# Revit family: Casement_36_E_Side_Hung_Standard
name_source: partatom
category: Windows
revit_build: Autodesk Revit 2014 (Build: 20130308_1515(x64)
units: mm (PartAtom-declared; Revit-internal decimal feet)

## types (18) — shared parameters
Aluminium Thickness = 1 mm  [stored 0.00328084 ft]
Area Pane Left Top = 0.52 m²
Bead SG Gap = 13 mm  [stored 0.0426509 ft]
Casement Dimension = 36 mm  [stored 0.11811 ft]
Custom Sash Height = 1154 mm  [stored 3.78609 ft]
Custom Sash Width = 554 mm  [stored 1.81759 ft]
DG Extrusion Start = 8 mm  [stored 0.0262467 ft]
DG Gasket Finish = Double Glazing Gasket Material
DG Thickness Calc = 4 mm  [stored 0.0131234 ft]
Default Sill Height = 800 mm  [stored 2.62467 ft]
Depth Bead = 22 mm  [stored 0.0721785 ft]
Description = Window 36mm, Type E side hung
Frame Center Offset = 18 mm  [stored 0.0590551 ft]
Height Panel 1 = 1139 mm  [stored 3.73688 ft]
Height Sash = 1124 mm  [stored 3.68766 ft]
Height Sash Opening = 1154 mm  [stored 3.78609 ft]
Length Transom = 540 mm  [stored 1.77165 ft]
Limit Fixed Pane Height Max = 1800 mm
Limit Fixed Pane Height Min = 200 mm  [stored 0.656168 ft]
Limit Fixed Pane Width Max = 1500 mm
Limit Fixed Pane Width Min = 200 mm  [stored 0.656168 ft]
Limit Sash Height Max = 1300 mm  [stored 4.26509 ft]
Limit Sash Height Min = 300 mm  [stored 0.984252 ft]
Limit Sash Width Max = 600 mm  [stored 1.9685 ft]
Limit Sash Width Min = 300 mm  [stored 0.984252 ft]
Limit Window Height Max = 1860 mm
Limit Window Height Min = 1430 mm  [stored 4.6916 ft]
Limit Window Width Max = 2130 mm
Limit Window Width Min = 830 mm  [stored 2.7231 ft]
Manufacturer = Crealco
Max System DG One Piece Thickness = 6 mm  [stored 0.019685 ft]
Max System DG Unit Thickness = 25 mm  [stored 0.082021 ft]
Model = Casement 36
Offset Bead SG Center Reversed = 18 mm  [stored 0.0590551 ft]
Offset Mullion Left = 570 mm  [stored 1.87008 ft]
Offset Panel 3 Bead Top = 1200 mm
Offset Panel 4 Left = 600 mm  [stored 1.9685 ft]
Offset Sash Left = 23 mm  [stored 0.0754593 ft]
Offset Sash Top = 23 mm  [stored 0.0754593 ft]
Offset Transom Top = 1170 mm
Offset Window Exterior = 18 mm  [stored 0.0590551 ft]
SG Gasket Thickness = 6 mm  [stored 0.019685 ft]
Sash Center Offset = 15 mm  [stored 0.0492126 ft]
Sash Overlap = 7 mm  [stored 0.0229659 ft]
Sash Spacing Inner = 8 mm  [stored 0.0262467 ft]
URL = http://www.crealco.co.za
Wall Closure = By host
Width Bead = 15 mm  [stored 0.0492126 ft]
Width Fixed Pane Bottom LHS = 540 mm  [stored 1.77165 ft]
Width Panel 1 = 540 mm  [stored 1.77165 ft]
Width Profile = 30 mm  [stored 0.0984252 ft]
Width Sash = 524 mm  [stored 1.71916 ft]
Width Sash Opening = 554 mm  [stored 1.81759 ft]
zero-valued in all types: Window Exterior Offset

## per-type parameters (varying)
- 36-0915S-1000Pa: Area Pane Left Bottom=0.13 m²; Area Pane Right=0.36 m²; Clearvue Insulated LowE SHGC Value=0.5; Clearvue Insulated LowE U Value=4.02; Clearvue Insulated SHGC Value=0.549; Clearvue Insulated U Value=4.53; Clearvue SHGC Value=0.622; Clearvue U Value=6.69; Custom Windload=1000 mm  [stored 3.28084 ft]; Custom Window Height=1490 mm; Custom Window Width=890 mm  [stored 2.91995 ft]; Depth Mullion=37 mm  [stored 0.121391 ft]; Energy Advantage SHGC Value=0.558; Energy Advantage U Value=5.22; Height=1490 mm; Height Fixed Pane Bottom LHS=260 mm  [stored 0.853018 ft]; Height Fixed Pane RHS=1430 mm  [stored 4.6916 ft]; Intruderprufe Insulated LowE SHGC Value=0.46; Intruderprufe Insulated LowE U Value=3.93; Intruderprufe Insulated SHGC Value=0.501; Intruderprufe Insulated U Value=4.41; Intruderprufe LowE SHGC Value=0.525; Intruderprufe LowE U Value=5.09; Intruderprufe SHGC Value=0.593; Intruderprufe U Value=6.53; Length Mullion=1490 mm; Max Pane Area=0.52 m²; Mullion Depth Windload Based=37 mm  [stored 0.121391 ft]; Width=890 mm  [stored 2.91995 ft]; Width Fixed Pane RHS=260 mm  [stored 0.853018 ft]; Windload Design=1000 mm  [stored 3.28084 ft]
- 36-1215S-1000Pa: Area Pane Left Bottom=0.13 m²; Area Pane Right=0.78 m²; Clearvue Insulated LowE SHGC Value=0.564; Clearvue Insulated LowE U Value=3.83; Clearvue Insulated SHGC Value=0.62; Clearvue Insulated U Value=4.43; Clearvue SHGC Value=0.704; Clearvue U Value=6.89; Custom Windload=1000 mm  [stored 3.28084 ft]; Custom Window Height=1490 mm; Custom Window Width=1190 mm  [stored 3.9042 ft]; Depth Mullion=54 mm  [stored 0.177165 ft]; Energy Advantage SHGC Value=0.631; Energy Advantage U Value=5.2; Height=1490 mm; Height Fixed Pane Bottom LHS=260 mm  [stored 0.853018 ft]; Height Fixed Pane RHS=1430 mm  [stored 4.6916 ft]; Intruderprufe Insulated LowE SHGC Value=0.521; Intruderprufe Insulated LowE U Value=3.75; Intruderprufe Insulated SHGC Value=0.569; Intruderprufe Insulated U Value=4.32; Intruderprufe LowE SHGC Value=0.59; Intruderprufe LowE U Value=5.09; Intruderprufe SHGC Value=0.671; Intruderprufe U Value=6.74; Length Mullion=1490 mm; Max Pane Area=0.78 m²; Mullion Depth Windload Based=54 mm  [stored 0.177165 ft]; Width=1190 mm  [stored 3.9042 ft]; Width Fixed Pane RHS=560 mm; Windload Design=1000 mm  [stored 3.28084 ft]
- 36-1515S-1000Pa: Area Pane Left Bottom=0.13 m²; Area Pane Right=1.21 m²; Clearvue Insulated LowE SHGC Value=0.606; Clearvue Insulated LowE U Value=3.65; Clearvue Insulated SHGC Value=0.666; Clearvue Insulated U Value=4.32; Clearvue SHGC Value=0.757; Clearvue U Value=6.99; Custom Windload=1000 mm  [stored 3.28084 ft]; Custom Window Height=1490 mm; Custom Window Width=1490 mm; Depth Mullion=54 mm  [stored 0.177165 ft]; Energy Advantage SHGC Value=0.679; Energy Advantage U Value=5.15; Height=1490 mm; Height Fixed Pane Bottom LHS=260 mm  [stored 0.853018 ft]; Height Fixed Pane RHS=1430 mm  [stored 4.6916 ft]; Intruderprufe Insulated LowE SHGC Value=0.559; Intruderprufe Insulated LowE U Value=3.57; Intruderprufe Insulated SHGC Value=0.612; Intruderprufe Insulated U Value=4.21; Intruderprufe LowE SHGC Value=0.634; Intruderprufe LowE U Value=5.03; Intruderprufe SHGC Value=0.721; Intruderprufe U Value=6.83; Length Mullion=1490 mm; Max Pane Area=1.21 m²; Mullion Depth Windload Based=54 mm  [stored 0.177165 ft]; Width=1490 mm; Width Fixed Pane RHS=860 mm  [stored 2.82152 ft]; Windload Design=1000 mm  [stored 3.28084 ft]
- 36-0918S-1000Pa: Area Pane Left Bottom=0.29 m²; Area Pane Right=0.43 m²; Clearvue Insulated LowE SHGC Value=0.536; Clearvue Insulated LowE U Value=4.2; Clearvue Insulated SHGC Value=0.588; Clearvue Insulated U Value=4.75; Clearvue SHGC Value=0.669; Clearvue U Value=7.05; Custom Windload=1000 mm  [stored 3.28084 ft]; Custom Window Height=1790 mm; Custom Window Width=890 mm  [stored 2.91995 ft]; Depth Mullion=54 mm  [stored 0.177165 ft]; Energy Advantage SHGC Value=0.599; Energy Advantage U Value=5.47; Height=1790 mm; Height Fixed Pane Bottom LHS=560 mm; Height Fixed Pane RHS=1730 mm; Intruderprufe Insulated LowE SHGC Value=0.497; Intruderprufe Insulated LowE U Value=4.11; Intruderprufe Insulated SHGC Value=0.54; Intruderprufe Insulated U Value=4.63; Intruderprufe LowE SHGC Value=0.562; Intruderprufe LowE U Value=5.53; Intruderprufe SHGC Value=0.638; Intruderprufe U Value=6.89; Length Mullion=1790 mm; Max Pane Area=0.52 m²; Mullion Depth Windload Based=54 mm  [stored 0.177165 ft]; Width=890 mm  [stored 2.91995 ft]; Width Fixed Pane RHS=260 mm  [stored 0.853018 ft]; Windload Design=1000 mm  [stored 3.28084 ft]
- 36-1218S-1000Pa: Area Pane Left Bottom=0.29 m²; Area Pane Right=0.95 m²; Clearvue Insulated LowE SHGC Value=0.623; Clearvue Insulated LowE U Value=4.03; Clearvue Insulated SHGC Value=0.684; Clearvue Insulated U Value=4.7; Clearvue SHGC Value=0.778; Clearvue U Value=7.42; Custom Windload=1000 mm  [stored 3.28084 ft]; Custom Window Height=1790 mm; Custom Window Width=1190 mm  [stored 3.9042 ft]; Depth Mullion=54 mm  [stored 0.177165 ft]; Energy Advantage SHGC Value=0.696; Energy Advantage U Value=5.55; Height=1790 mm; Height Fixed Pane Bottom LHS=560 mm; Height Fixed Pane RHS=1730 mm; Intruderprufe Insulated LowE SHGC Value=0.575; Intruderprufe Insulated LowE U Value=3.94; Intruderprufe Insulated SHGC Value=0.628; Intruderprufe Insulated U Value=4.58; Intruderprufe LowE SHGC Value=0.651; Intruderprufe LowE U Value=5.43; Intruderprufe SHGC Value=0.74; Intruderprufe U Value=7.25; Length Mullion=1790 mm; Max Pane Area=0.95 m²; Mullion Depth Windload Based=54 mm  [stored 0.177165 ft]; Width=1190 mm  [stored 3.9042 ft]; Width Fixed Pane RHS=560 mm; Windload Design=1000 mm  [stored 3.28084 ft]
- 36-1518S-1000Pa: Area Pane Left Bottom=0.29 m²; Area Pane Right=1.46 m²; Clearvue Insulated LowE SHGC Value=0.68; Clearvue Insulated LowE U Value=3.91; Clearvue Insulated SHGC Value=0.748; Clearvue Insulated U Value=4.66; Clearvue SHGC Value=0; Clearvue U Value=7.9; Custom Windload=1000 mm  [stored 3.28084 ft]; Custom Window Height=1790 mm; Custom Window Width=1490 mm; Depth Mullion=70 mm  [stored 0.229659 ft]; Energy Advantage SHGC Value=0; Energy Advantage U Value=7.9; Height=1790 mm; Height Fixed Pane Bottom LHS=560 mm; Height Fixed Pane RHS=1730 mm; Intruderprufe Insulated LowE SHGC Value=0.627; Intruderprufe Insulated LowE U Value=3.83; Intruderprufe Insulated SHGC Value=0.688; Intruderprufe Insulated U Value=4.55; Intruderprufe LowE SHGC Value=0.711; Intruderprufe LowE U Value=5.48; Intruderprufe SHGC Value=0.808; Intruderprufe U Value=7.5; Length Mullion=1790 mm; Max Pane Area=1.46 m²; Mullion Depth Windload Based=70 mm  [stored 0.229659 ft]; Width=1490 mm; Width Fixed Pane RHS=860 mm  [stored 2.82152 ft]; Windload Design=1000 mm  [stored 3.28084 ft]
- 36-0915S-1500Pa: Area Pane Left Bottom=0.13 m²; Area Pane Right=0.36 m²; Clearvue Insulated LowE SHGC Value=0.498; Clearvue Insulated LowE U Value=4.11; Clearvue Insulated SHGC Value=0.546; Clearvue Insulated U Value=4.62; Clearvue SHGC Value=0.62; Clearvue U Value=3.73; Custom Windload=1500 mm; Custom Window Height=1490 mm; Custom Window Width=890 mm  [stored 2.91995 ft]; Depth Mullion=54 mm  [stored 0.177165 ft]; Energy Advantage SHGC Value=0.556; Energy Advantage U Value=5.29; Height=1490 mm; Height Fixed Pane Bottom LHS=260 mm  [stored 0.853018 ft]; Height Fixed Pane RHS=1430 mm  [stored 4.6916 ft]; Intruderprufe Insulated LowE SHGC Value=0.461; Intruderprufe Insulated LowE U Value=4.02; Intruderprufe Insulated SHGC Value=0.5; Intruderprufe Insulated U Value=4.5; Intruderprufe LowE SHGC Value=0.522; Intruderprufe LowE U Value=5.17; Intruderprufe SHGC Value=0.592; Intruderprufe U Value=6.58; Length Mullion=1490 mm; Max Pane Area=0.52 m²; Mullion Depth Windload Based=54 mm  [stored 0.177165 ft]; Width=890 mm  [stored 2.91995 ft]; Width Fixed Pane RHS=260 mm  [stored 0.853018 ft]; Windload Design=1500 mm
- 36-0915S-2000Pa: Area Pane Left Bottom=0.13 m²; Area Pane Right=0.36 m²; Clearvue Insulated LowE SHGC Value=0.498; Clearvue Insulated LowE U Value=4.11; Clearvue Insulated SHGC Value=0.546; Clearvue Insulated U Value=4.62; Clearvue SHGC Value=0.62; Clearvue U Value=3.73; Custom Windload=2000 mm; Custom Window Height=1490 mm; Custom Window Width=890 mm  [stored 2.91995 ft]; Depth Mullion=54 mm  [stored 0.177165 ft]; Energy Advantage SHGC Value=0.556; Energy Advantage U Value=5.29; Height=1490 mm; Height Fixed Pane Bottom LHS=260 mm  [stored 0.853018 ft]; Height Fixed Pane RHS=1430 mm  [stored 4.6916 ft]; Intruderprufe Insulated LowE SHGC Value=0.461; Intruderprufe Insulated LowE U Value=4.02; Intruderprufe Insulated SHGC Value=0.5; Intruderprufe Insulated U Value=4.5; Intruderprufe LowE SHGC Value=0.522; Intruderprufe LowE U Value=5.17; Intruderprufe SHGC Value=0.592; Intruderprufe U Value=6.58; Length Mullion=1490 mm; Max Pane Area=0.52 m²; Mullion Depth Windload Based=54 mm  [stored 0.177165 ft]; Width=890 mm  [stored 2.91995 ft]; Width Fixed Pane RHS=260 mm  [stored 0.853018 ft]; Windload Design=2000 mm
- 36-1215S-1500Pa: Area Pane Left Bottom=0.13 m²; Area Pane Right=0.78 m²; Clearvue Insulated LowE SHGC Value=0.564; Clearvue Insulated LowE U Value=3.83; Clearvue Insulated SHGC Value=0.62; Clearvue Insulated U Value=4.43; Clearvue SHGC Value=0.704; Clearvue U Value=6.89; Custom Windload=1500 mm; Custom Window Height=1490 mm; Custom Window Width=1190 mm  [stored 3.9042 ft]; Depth Mullion=54 mm  [stored 0.177165 ft]; Energy Advantage SHGC Value=0.631; Energy Advantage U Value=5.2; Height=1490 mm; Height Fixed Pane Bottom LHS=260 mm  [stored 0.853018 ft]; Height Fixed Pane RHS=1430 mm  [stored 4.6916 ft]; Intruderprufe Insulated LowE SHGC Value=0.521; Intruderprufe Insulated LowE U Value=3.75; Intruderprufe Insulated SHGC Value=0.569; Intruderprufe Insulated U Value=4.32; Intruderprufe LowE SHGC Value=0.59; Intruderprufe LowE U Value=5.09; Intruderprufe SHGC Value=0.671; Intruderprufe U Value=6.74; Length Mullion=1490 mm; Max Pane Area=0.78 m²; Mullion Depth Windload Based=54 mm  [stored 0.177165 ft]; Width=1190 mm  [stored 3.9042 ft]; Width Fixed Pane RHS=560 mm; Windload Design=1500 mm
- 36-1215S-2000Pa: Area Pane Left Bottom=0.13 m²; Area Pane Right=0.78 m²; Clearvue Insulated LowE SHGC Value=0.564; Clearvue Insulated LowE U Value=3.83; Clearvue Insulated SHGC Value=0.62; Clearvue Insulated U Value=4.43; Clearvue SHGC Value=0.704; Clearvue U Value=6.89; Custom Windload=2000 mm; Custom Window Height=1490 mm; Custom Window Width=1190 mm  [stored 3.9042 ft]; Depth Mullion=54 mm  [stored 0.177165 ft]; Energy Advantage SHGC Value=0.631; Energy Advantage U Value=5.2; Height=1490 mm; Height Fixed Pane Bottom LHS=260 mm  [stored 0.853018 ft]; Height Fixed Pane RHS=1430 mm  [stored 4.6916 ft]; Intruderprufe Insulated LowE SHGC Value=0.521; Intruderprufe Insulated LowE U Value=3.75; Intruderprufe Insulated SHGC Value=0.569; Intruderprufe Insulated U Value=4.32; Intruderprufe LowE SHGC Value=0.59; Intruderprufe LowE U Value=5.09; Intruderprufe SHGC Value=0.671; Intruderprufe U Value=6.74; Length Mullion=1490 mm; Max Pane Area=0.78 m²; Mullion Depth Windload Based=54 mm  [stored 0.177165 ft]; Width=1190 mm  [stored 3.9042 ft]; Width Fixed Pane RHS=560 mm; Windload Design=2000 mm
- 36-1515S-1500Pa: Area Pane Left Bottom=0.13 m²; Area Pane Right=1.21 m²; Clearvue Insulated LowE SHGC Value=0.606; Clearvue Insulated LowE U Value=3.65; Clearvue Insulated SHGC Value=0.666; Clearvue Insulated U Value=4.32; Clearvue SHGC Value=0.757; Clearvue U Value=6.99; Custom Windload=1500 mm; Custom Window Height=1490 mm; Custom Window Width=1490 mm; Depth Mullion=54 mm  [stored 0.177165 ft]; Energy Advantage SHGC Value=0.679; Energy Advantage U Value=5.15; Height=1490 mm; Height Fixed Pane Bottom LHS=260 mm  [stored 0.853018 ft]; Height Fixed Pane RHS=1430 mm  [stored 4.6916 ft]; Intruderprufe Insulated LowE SHGC Value=0.559; Intruderprufe Insulated LowE U Value=3.57; Intruderprufe Insulated SHGC Value=0.612; Intruderprufe Insulated U Value=4.21; Intruderprufe LowE SHGC Value=0.634; Intruderprufe LowE U Value=5.03; Intruderprufe SHGC Value=0.721; Intruderprufe U Value=6.83; Length Mullion=1490 mm; Max Pane Area=1.21 m²; Mullion Depth Windload Based=54 mm  [stored 0.177165 ft]; Width=1490 mm; Width Fixed Pane RHS=860 mm  [stored 2.82152 ft]; Windload Design=1500 mm
- 36-1515S-2000Pa: Area Pane Left Bottom=0.13 m²; Area Pane Right=1.21 m²; Clearvue Insulated LowE SHGC Value=0.606; Clearvue Insulated LowE U Value=3.65; Clearvue Insulated SHGC Value=0.666; Clearvue Insulated U Value=4.32; Clearvue SHGC Value=0.757; Clearvue U Value=6.99; Custom Windload=2000 mm; Custom Window Height=1490 mm; Custom Window Width=1490 mm; Depth Mullion=54 mm  [stored 0.177165 ft]; Energy Advantage SHGC Value=0.679; Energy Advantage U Value=5.15; Height=1490 mm; Height Fixed Pane Bottom LHS=260 mm  [stored 0.853018 ft]; Height Fixed Pane RHS=1430 mm  [stored 4.6916 ft]; Intruderprufe Insulated LowE SHGC Value=0.559; Intruderprufe Insulated LowE U Value=3.57; Intruderprufe Insulated SHGC Value=0.612; Intruderprufe Insulated U Value=4.21; Intruderprufe LowE SHGC Value=0.634; Intruderprufe LowE U Value=5.03; Intruderprufe SHGC Value=0.721; Intruderprufe U Value=6.83; Length Mullion=1490 mm; Max Pane Area=1.21 m²; Mullion Depth Windload Based=54 mm  [stored 0.177165 ft]; Width=1490 mm; Width Fixed Pane RHS=860 mm  [stored 2.82152 ft]; Windload Design=2000 mm
- 36-0918S-1500Pa: Area Pane Left Bottom=0.29 m²; Area Pane Right=0.43 m²; Clearvue Insulated LowE SHGC Value=0.536; Clearvue Insulated LowE U Value=4.2; Clearvue Insulated SHGC Value=0.588; Clearvue Insulated U Value=4.75; Clearvue SHGC Value=0.669; Clearvue U Value=7.05; Custom Windload=1500 mm; Custom Window Height=1790 mm; Custom Window Width=890 mm  [stored 2.91995 ft]; Depth Mullion=54 mm  [stored 0.177165 ft]; Energy Advantage SHGC Value=0.599; Energy Advantage U Value=5.47; Height=1790 mm; Height Fixed Pane Bottom LHS=560 mm; Height Fixed Pane RHS=1730 mm; Intruderprufe Insulated LowE SHGC Value=0.497; Intruderprufe Insulated LowE U Value=4.11; Intruderprufe Insulated SHGC Value=0.54; Intruderprufe Insulated U Value=4.63; Intruderprufe LowE SHGC Value=0.562; Intruderprufe LowE U Value=5.53; Intruderprufe SHGC Value=0.638; Intruderprufe U Value=6.89; Length Mullion=1790 mm; Max Pane Area=0.52 m²; Mullion Depth Windload Based=54 mm  [stored 0.177165 ft]; Width=890 mm  [stored 2.91995 ft]; Width Fixed Pane RHS=260 mm  [stored 0.853018 ft]; Windload Design=1500 mm
- 36-0918S-2000Pa: Area Pane Left Bottom=0.29 m²; Area Pane Right=0.43 m²; Clearvue Insulated LowE SHGC Value=0.536; Clearvue Insulated LowE U Value=4.2; Clearvue Insulated SHGC Value=0.588; Clearvue Insulated U Value=4.75; Clearvue SHGC Value=0.669; Clearvue U Value=7.05; Custom Windload=2000 mm; Custom Window Height=1790 mm; Custom Window Width=890 mm  [stored 2.91995 ft]; Depth Mullion=54 mm  [stored 0.177165 ft]; Energy Advantage SHGC Value=0.599; Energy Advantage U Value=5.47; Height=1790 mm; Height Fixed Pane Bottom LHS=560 mm; Height Fixed Pane RHS=1730 mm; Intruderprufe Insulated LowE SHGC Value=0.497; Intruderprufe Insulated LowE U Value=4.11; Intruderprufe Insulated SHGC Value=0.54; Intruderprufe Insulated U Value=4.63; Intruderprufe LowE SHGC Value=0.562; Intruderprufe LowE U Value=5.53; Intruderprufe SHGC Value=0.638; Intruderprufe U Value=6.89; Length Mullion=1790 mm; Max Pane Area=0.52 m²; Mullion Depth Windload Based=54 mm  [stored 0.177165 ft]; Width=890 mm  [stored 2.91995 ft]; Width Fixed Pane RHS=260 mm  [stored 0.853018 ft]; Windload Design=2000 mm
- 36-1218S-1500Pa: Area Pane Left Bottom=0.29 m²; Area Pane Right=0.95 m²; Clearvue Insulated LowE SHGC Value=0.623; Clearvue Insulated LowE U Value=4.03; Clearvue Insulated SHGC Value=0.684; Clearvue Insulated U Value=4.7; Clearvue SHGC Value=0.778; Clearvue U Value=7.42; Custom Windload=1500 mm; Custom Window Height=1790 mm; Custom Window Width=1190 mm  [stored 3.9042 ft]; Depth Mullion=70 mm  [stored 0.229659 ft]; Energy Advantage SHGC Value=0.696; Energy Advantage U Value=5.55; Height=1790 mm; Height Fixed Pane Bottom LHS=560 mm; Height Fixed Pane RHS=1730 mm; Intruderprufe Insulated LowE SHGC Value=0.575; Intruderprufe Insulated LowE U Value=3.94; Intruderprufe Insulated SHGC Value=0.628; Intruderprufe Insulated U Value=4.58; Intruderprufe LowE SHGC Value=0.651; Intruderprufe LowE U Value=5.43; Intruderprufe SHGC Value=0.74; Intruderprufe U Value=7.25; Length Mullion=1790 mm; Max Pane Area=0.95 m²; Mullion Depth Windload Based=70 mm  [stored 0.229659 ft]; Width=1190 mm  [stored 3.9042 ft]; Width Fixed Pane RHS=560 mm; Windload Design=1500 mm
- 36-1218S-2000Pa: Area Pane Left Bottom=0.29 m²; Area Pane Right=0.95 m²; Clearvue Insulated LowE SHGC Value=0.623; Clearvue Insulated LowE U Value=4.03; Clearvue Insulated SHGC Value=0.684; Clearvue Insulated U Value=4.7; Clearvue SHGC Value=0.778; Clearvue U Value=7.42; Custom Windload=2000 mm; Custom Window Height=1790 mm; Custom Window Width=1190 mm  [stored 3.9042 ft]; Depth Mullion=70 mm  [stored 0.229659 ft]; Energy Advantage SHGC Value=0.696; Energy Advantage U Value=5.55; Height=1790 mm; Height Fixed Pane Bottom LHS=560 mm; Height Fixed Pane RHS=1730 mm; Intruderprufe Insulated LowE SHGC Value=0.575; Intruderprufe Insulated LowE U Value=3.94; Intruderprufe Insulated SHGC Value=0.628; Intruderprufe Insulated U Value=4.58; Intruderprufe LowE SHGC Value=0.651; Intruderprufe LowE U Value=5.43; Intruderprufe SHGC Value=0.74; Intruderprufe U Value=7.25; Length Mullion=1790 mm; Max Pane Area=0.95 m²; Mullion Depth Windload Based=70 mm  [stored 0.229659 ft]; Width=1190 mm  [stored 3.9042 ft]; Width Fixed Pane RHS=560 mm; Windload Design=2000 mm
- 36-1518S-1500Pa: Area Pane Left Bottom=0.29 m²; Area Pane Right=1.46 m²; Clearvue Insulated LowE SHGC Value=0.68; Clearvue Insulated LowE U Value=3.91; Clearvue Insulated SHGC Value=0.748; Clearvue Insulated U Value=4.66; Clearvue SHGC Value=0; Clearvue U Value=7.9; Custom Windload=1500 mm; Custom Window Height=1790 mm; Custom Window Width=1490 mm; Depth Mullion=70 mm  [stored 0.229659 ft]; Energy Advantage SHGC Value=0; Energy Advantage U Value=7.9; Height=1790 mm; Height Fixed Pane Bottom LHS=560 mm; Height Fixed Pane RHS=1730 mm; Intruderprufe Insulated LowE SHGC Value=0.627; Intruderprufe Insulated LowE U Value=3.83; Intruderprufe Insulated SHGC Value=0.688; Intruderprufe Insulated U Value=4.55; Intruderprufe LowE SHGC Value=0.711; Intruderprufe LowE U Value=5.48; Intruderprufe SHGC Value=0.808; Intruderprufe U Value=7.5; Length Mullion=1790 mm; Max Pane Area=1.46 m²; Mullion Depth Windload Based=70 mm  [stored 0.229659 ft]; Width=1490 mm; Width Fixed Pane RHS=860 mm  [stored 2.82152 ft]; Windload Design=1500 mm
- 36-1518S-2000Pa: Area Pane Left Bottom=0.29 m²; Area Pane Right=1.46 m²; Clearvue Insulated LowE SHGC Value=0.681; Clearvue Insulated LowE U Value=3.94; Clearvue Insulated SHGC Value=0.748; Clearvue Insulated U Value=4.69; Clearvue SHGC Value=0; Clearvue U Value=7.9; Custom Windload=2000 mm; Custom Window Height=1790 mm; Custom Window Width=1490 mm; Depth Mullion=90 mm  [stored 0.295276 ft]; Energy Advantage SHGC Value=0; Energy Advantage U Value=7.9; Height=1790 mm; Height Fixed Pane Bottom LHS=560 mm; Height Fixed Pane RHS=1730 mm; Intruderprufe Insulated LowE SHGC Value=0.627; Intruderprufe Insulated LowE U Value=3.87; Intruderprufe Insulated SHGC Value=0.688; Intruderprufe Insulated U Value=4.58; Intruderprufe LowE SHGC Value=0.713; Intruderprufe LowE U Value=5.53; Intruderprufe SHGC Value=0.811; Intruderprufe U Value=7.55; Length Mullion=1790 mm; Max Pane Area=1.46 m²; Mullion Depth Windload Based=90 mm  [stored 0.295276 ft]; Width=1490 mm; Width Fixed Pane RHS=860 mm  [stored 2.82152 ft]; Windload Design=2000 mm

note: [stored X ft] marks values corroborated as IEEE doubles in the binary element streams (Revit-internal decimal feet)

## geometry (parser evidence)
native form markers: Blend x4, Extrusion x1, Sweep x28
no freeform markers — native parametric forms only
